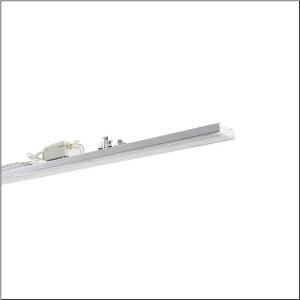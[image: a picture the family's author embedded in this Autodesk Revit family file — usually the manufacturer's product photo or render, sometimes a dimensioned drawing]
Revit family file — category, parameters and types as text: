
# Revit family: licross_r__11_recessed_mo_51te117n485g_c7ea
name_source: partatom
category: Lighting Fixtures
units: mm (PartAtom-declared; Revit-internal decimal feet)

## family parameters
Cut with Voids When Loaded = No
Host = Face
Light Source = No
Part Type = Normal
Room Calculation Point = No
Round Connector Dimension = Use Diameter
Shared = No

## types (1)
- Licross® 11 Recessed MO (1 x LED, 8810 lm, 48.5 W, 4000K)
    Apparent Load = 49 VA
    CIE Flux Codes = 89 96 99 100 100
    Color Rendering = 80
    Color Temperature = 4000K
    Default Elevation = 1800 mm
    Description = Licross® 11 Recessed MO, luminaire insert, of sheet steel, galvanised, coil coated, white, length: 1.500mm, width: 66mm, height: 67mm, LED rated luminous flux: 8.820lm, light colour: 840, SDCM (Standard Deviation of Colour Matching)MacAdam ≤ 2 SDCM (initial), control gear: ON/OFF, with plug, 3-pole, with phase selection, mains connection: 220..240V, AC, 50/60Hz, rated input power: 49W, internal wiring halogen-free, primary light control with lens, of plastic, primary optical cover: cover, of PMMA, light emission: direct distribution, primary light characteristic: symmetric, protection rating (complete): IP54, insulation class (complete): insulation class I (protective earthing), certification: CE, ENEC, VDE, UKCA, protection symbol: D if used in an environment with non-conductive dust loads with corresponding accessories, impact resistance: IK06, permissible ambient temperature for indoor applications: -35..+35°C, corresponds to IFS (International Featured Standards) requirements for safety and quality in the food industry, reducing of maximum allowable ambient temperature of 5°C with ceiling mounting, packaging unit: 1 piece
    Height = 58 mm
    Lamp = 1 x LED
    Lamp Light Flux = 8810 lm
    Lamp Power = 48.5 W
    Lamp count = 1
    Length = 1500 mm
    Luminous efficacy = 182 lm/W
    Manufacturer = Siteco
    ModVariant = No
    Model = 51TE117N485G
    Mounting Place = Ceiling
    Mounting Type = Pendant
    Number of Poles = 1
    OnlyDefault = Yes
    Power Factor = 1
    Product Name = Licross® 11 Recessed MO
    Product group = luminaire insert | ceiling pendant
    ProductGroupID = 901
    Protection Class = Protection class I
    Protection Degree = IP 54
    RLX_Detail_Level = 1
    RLX_Emergency_Light_Flux = 0 lm
    RLX_Emergency_Type = 0
    RLX_Emergency_Type_DB = No
    RlxData = <blob elided: 20845 chars, md5=d6e3dcb2>
    Socket = socket
    Standby Power = 0 W
    System Light Flux = 8810 lm
    System Power = 49 W
    Type Comments = Product without accessories
    Type Image = l_1296930.jpg
    URL = http://relux.com
    VarID = ---
    Voltage = 0 V
    Weight = 0.00 kg
    Width = 66 mm

## geometry (parser evidence)
native form markers: Blend x4, Sweep x11
no freeform markers — native parametric forms only
